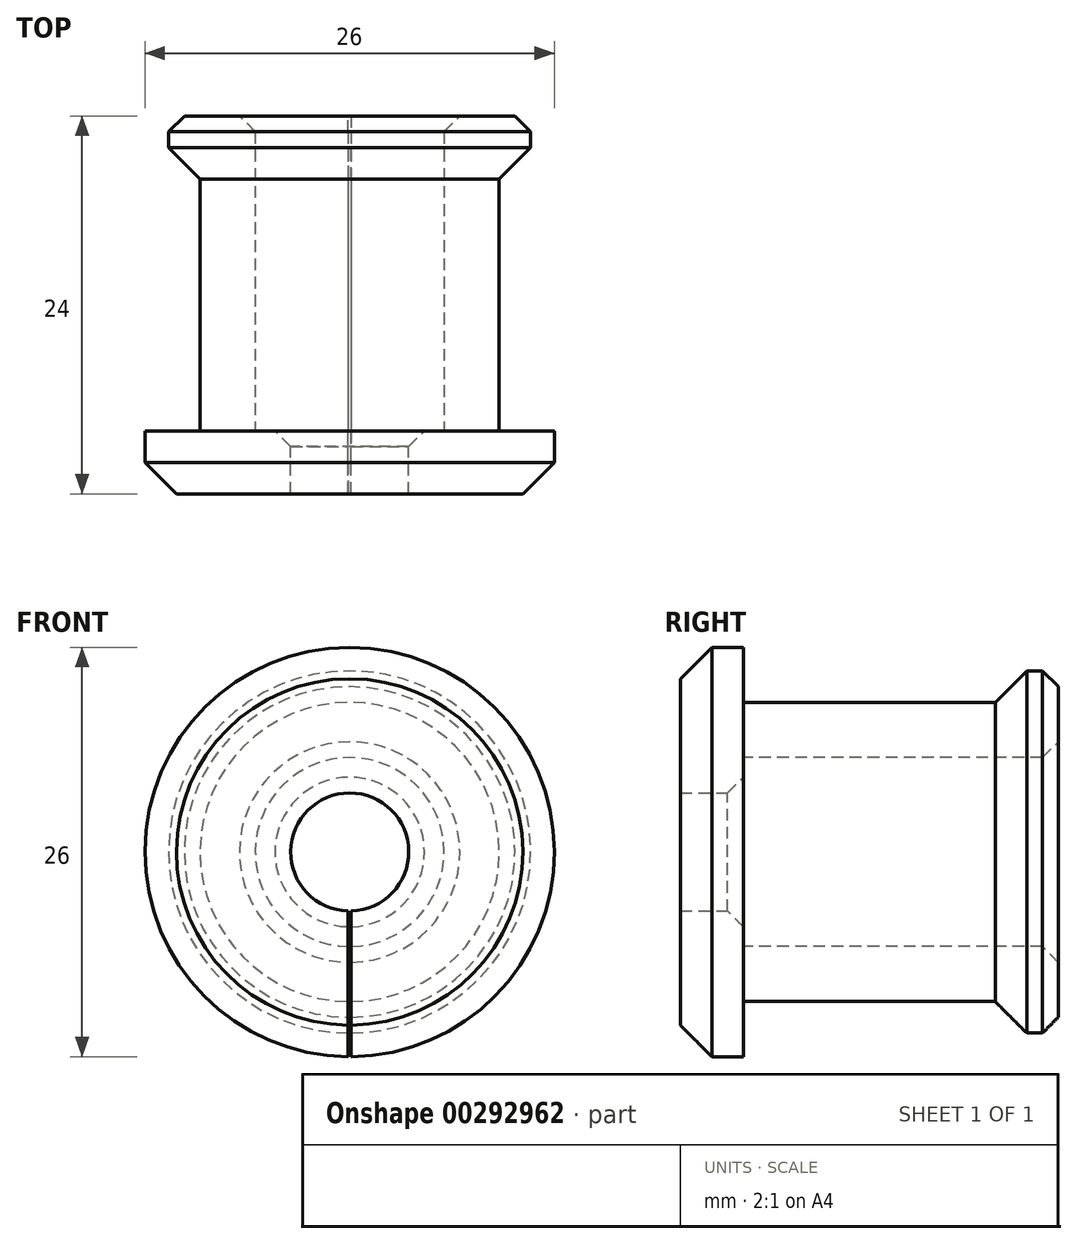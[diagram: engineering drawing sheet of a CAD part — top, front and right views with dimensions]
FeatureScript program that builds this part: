
annotation { "Feature Type Name" : "Feature", "Feature Type Description" : "" }
export const myFeature = defineFeature(function(context is Context, id is Id, definition is map)
    precondition{}
    {
        {
            var Q0;
            Q0=qCreatedBy(makeId("Front.planeOp"),FACE);
            var sketch = newSketch(context, id + "F0", { "sketchPlane" : qUnion([Q0])});
            skCircle(sketch, "E0", {"center": v(0, 0) * mm, "radius": 9.5 * mm});
            skCircle(sketch, "E1", {"center": v(0, 0) * mm, "radius": 13 * mm});
            skCircle(sketch, "E2", {"center": v(0, 0) * mm, "radius": 3.75 * mm});
            skCircle(sketch, "E3", {"center": v(0, 0) * mm, "radius": 11.5 * mm});
            skCircle(sketch, "E4", {"center": v(0, 0) * mm, "radius": 6 * mm});
            skSolve(sketch);
        }
        {
            var Q0;
            Q0=makeQuery(id+"F0.imprint","IMPRINT",FACE,{"disambiguationData":[TD([[makeQuery(id+"F0.imprint","IMPRINT",EDGE,{"derivedFrom":sQuery(id+"F0.wireOp",EDGE,"E1")}),1.0]])]});
            var Q1;
            Q1=makeQuery(id+"F0.imprint","IMPRINT",FACE,{"disambiguationData":[TD([[makeQuery(id+"F0.imprint","IMPRINT",EDGE,{"derivedFrom":sQuery(id+"F0.wireOp",EDGE,"E0")}),-1.0]])]});
            var Q2;
            Q2=makeQuery(id+"F0.imprint","IMPRINT",FACE,{"disambiguationData":[TD([[makeQuery(id+"F0.imprint","IMPRINT",EDGE,{"derivedFrom":sQuery(id+"F0.wireOp",EDGE,"E0")}),1.0]])]});
            var Q3;
            Q3=makeQuery(id+"F0.imprint","IMPRINT",FACE,{"disambiguationData":[TD([[makeQuery(id+"F0.imprint","IMPRINT",EDGE,{"derivedFrom":sQuery(id+"F0.wireOp",EDGE,"E2")}),-1.0]])]});
            extrude(context, id + "F1", {"entities" : qUnion([Q0, Q1, Q2, Q3]), "depth" : 4 * mm});
        }
        {
            var Q0;
            Q0=makeQuery(id+"F0.imprint","IMPRINT",FACE,{"disambiguationData":[TD([[makeQuery(id+"F0.imprint","IMPRINT",EDGE,{"derivedFrom":sQuery(id+"F0.wireOp",EDGE,"E0")}),1.0]])]});
            extrude(context, id + "F2", {"entities" : qUnion([Q0]), "operationType" : NewBodyOperationType.ADD, "oppositeDirection" : true, "depth" : 16 * mm});
        }
        {
            var Q0;
            Q0=makeQuery(id+"F2.opExtrude","CAP_FACE",FACE,{"disambiguationData":[OSD([sQuery(id+"F0.wireOp",EDGE,"E0"),sQuery(id+"F0.wireOp",EDGE,"E4")])],"isStart":false});
            cPlane(context, id + "F3", {"entities" : qUnion([Q0]), "cplaneType" : CPlaneType.OFFSET, "offset" : 0 * mm, "width" : 150 * mm, "height" : 150 * mm});
        }
        {
            var Q0;
            Q0=qCreatedBy(id+"F3.planeOp",FACE);
            var sketch = newSketch(context, id + "F4", { "sketchPlane" : qUnion([Q0])});
            skCircle(sketch, "E5", {"center": v(0, 0) * mm, "radius": 11.5 * mm});
            skCircle(sketch, "E6", {"center": v(0, 0) * mm, "radius": 6 * mm});
            skSolve(sketch);
        }
        {
            var Q0;
            Q0=makeQuery(id+"F4.imprint","IMPRINT",FACE,{"disambiguationData":[TD([[makeQuery(id+"F4.imprint","IMPRINT",EDGE,{"derivedFrom":sQuery(id+"F4.wireOp",EDGE,"E5")}),1.0]])]});
            extrude(context, id + "F5", {"entities" : qUnion([Q0]), "operationType" : NewBodyOperationType.ADD, "depth" : 4 * mm});
        }
        {
            var Q0;
            Q0=makeQuery(id+"F1.opExtrude","CAP_EDGE",EDGE,{"disambiguationData":[OSD([sQuery(id+"F0.wireOp",EDGE,"E1")])],"isStart":false});
            chamfer(context, id + "F6", {"entities" : qUnion([Q0]), "width" : 2 * mm, "tangentPropagation" : true});
        }
        {
            var Q0;
            Q0=makeQuery(id+"F5.opExtrude","CAP_EDGE",EDGE,{"disambiguationData":[OSD([sQuery(id+"F4.wireOp",EDGE,"E6")])],"isStart":false});
            var Q1;
            Q1=makeQuery(id+"F1.opExtrude","CAP_EDGE",EDGE,{"disambiguationData":[OSD([sQuery(id+"F0.wireOp",EDGE,"E2")])],"isStart":true});
            var Q2;
            Q2=makeQuery(id+"F5.opExtrude","CAP_EDGE",EDGE,{"disambiguationData":[OSD([sQuery(id+"F4.wireOp",EDGE,"E5")])],"isStart":false});
            chamfer(context, id + "F7", {"entities" : qUnion([Q0, Q1, Q2]), "width" : 1 * mm, "tangentPropagation" : true});
        }
        {
            var Q0;
            Q0=makeQuery(id+"F5.opExtrude","CAP_EDGE",EDGE,{"disambiguationData":[OSD([sQuery(id+"F4.wireOp",EDGE,"E5")])],"isStart":true});
            chamfer(context, id + "F8", {"entities" : qUnion([Q0]), "width" : 2 * mm, "tangentPropagation" : true});
        }
        {
            var Q0;
            Q0=qCreatedBy(makeId("Front.planeOp"),FACE);
            var sketch = newSketch(context, id + "F9", { "sketchPlane" : qUnion([Q0])});
            skLineSegment(sketch, "E7", {"start": v(-0.1, 0) * mm, "end": v(0.1, 0) * mm});
            skLineSegment(sketch, "E8", {"start": v(0.1, 0) * mm, "end": v(0.1, -20) * mm});
            skLineSegment(sketch, "E9", {"start": v(0.1, -20) * mm, "end": v(-0.1, -20) * mm});
            skLineSegment(sketch, "E10", {"start": v(-0.1, -20) * mm, "end": v(-0.1, 0) * mm});
            skSolve(sketch);
        }
        {
            var Q0;
            Q0=qSketchRegion(id+"F9",true);
            extrude(context, id + "F10", {"entities" : qUnion([Q0]), "operationType" : NewBodyOperationType.REMOVE, "endBound" : BoundingType.SYMMETRIC, "oppositeDirection" : true, "depth" : 50 * mm});
        }
    });
